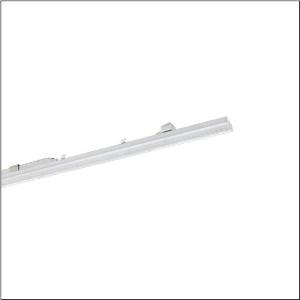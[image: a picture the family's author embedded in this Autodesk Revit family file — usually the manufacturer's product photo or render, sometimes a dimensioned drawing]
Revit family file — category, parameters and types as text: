
# Revit family: tl_l_5wd7a8f0b2b5
name_source: partatom
category: Lighting Fixtures
units: mm (PartAtom-declared; Revit-internal decimal feet)

## family parameters
Cut with Voids When Loaded = No
Host = Face
Light Source = No
Part Type = Normal
Room Calculation Point = No
Round Connector Dimension = Use Diameter
Shared = No

## types (1)
- TL L (1 x LED, 4990 lm, 30 W, 4000K)
    Apparent Load = 30 VA
    CIE Flux Codes = 49 84 98 100 100
    Color Rendering = 80
    Color Temperature = 4000K
    Default Elevation = 1800 mm
    Description = TL L, luminaire insert, of sheet steel, galvanised, coil coated, white, length: 1.500mm, width: 66mm, height: 67mm, micro fuse,LED rated luminous flux: 4.990lm, light colour: 840, control gear: 4..20mA, with terminal, 5-pole, mains connection: 230..240V, AC, 50/60Hz, rated input power: 30W, primary optical cover: cover, of PMMA, light emission: direct distribution, protection rating (complete): as luminaire, insulation class (complete): insulation class I (protective earthing), certification: CE, impact resistance: IK06, permissible ambient temperature for indoor applications: -25..+35°C, packaging unit: 1 piece
    Height = 120 mm
    Lamp = 1 x LED
    Lamp Light Flux = 4990 lm
    Lamp Power = 30 W
    Lamp count = 1
    Length = 1690 mm
    Luminous efficacy = 166 lm/W
    Manufacturer = Siteco
    ModVariant = No
    Model = 5WD7A8F0B2B5
    Mounting Place = Ceiling
    Mounting Type = Pendant
    Number of Poles = 1
    OnlyDefault = Yes
    Power Factor = 1
    Product Name = TL L
    Product group = luminaire insert
    ProductGroupID = 901
    Protection Class = Protection class I
    Protection Degree = Degree of protection
    RLX_Detail_Level = 1
    RLX_Emergency_Light_Flux = 0 lm
    RLX_Emergency_Type = 0
    RLX_Emergency_Type_DB = No
    RlxData = <blob elided: 14109 chars, md5=b712d095>
    Socket = socket
    Standby Power = 0 W
    System Light Flux = 4990 lm
    System Power = 30 W
    Type Comments = Product without accessories
    Type Image = l_1294382.jpg
    URL = http://relux.com
    VarID = ---
    Voltage = 0 V
    Weight = 0.00 kg
    Width = 208 mm

## geometry (parser evidence)
native form markers: Sweep x12
no freeform markers — native parametric forms only
